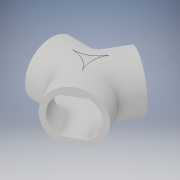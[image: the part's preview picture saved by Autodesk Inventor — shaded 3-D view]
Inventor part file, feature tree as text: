
AUTODESK INVENTOR PART (.ipt)
format: ipt  version: 2017 (Build 210142000, 142)  size: 393,216 bytes
history: native  units: in
note: dims shown in document units (in); Inventor stores cm internally (conversion verified against a paired STEP export)
features: sketch x5, extrude x4, other x2, pattern_circular x2, sweep x2
ambient origin geometry x8: Origin, YZ Plane, XZ Plane, XY Plane, X Axis, Y Axis, Z Axis, Center Point
bodies: Solid1 (feature_tree), Solid2 (feature_tree), Solid3 (feature_tree)
feature tree (15):
  sketch  "Sketch1"  dims[d10=6.6667in d11=4.0in d12=4.0in d13=0.0in d14=9.7746in]
  extrude  "corridor"  Depth=9.7746in
  extrude  "light"  Depth=1.1811in TaperAngle=360.0deg
  other  "found rotaion axis"
  other  "rotaion axis"
  pattern_circular  "other corridors"  Count=3 Angle=360.0deg
  sketch  "Sketch5"  dims[d24=0.0in d25=0.0in d26=1.1811in d27=360.0deg]
  sketch  "Sketch4"  dims[d15=2.8217in d16=1.1811in d17=360.0deg]
  sweep  "curve edjes"
  sweep  "light curve"
  pattern_circular  "repeat curve edjes"  [2 undecoded]
  extrude  "top hole fill in"  Depth=1.429in TaperAngle=0.0deg
  extrude  "bottom hole fill up"  TaperAngle=0.0deg  [1 undecoded]
  sketch  "Sketch7"  dims[d37=1.554in d38=0.0in d46=1.0in]
  sketch  "Sketch9"  dims[d51=0.5833in d52=0.0625in d53=0.0625in d54=0.125in d55=0.0625in d61=0.25in d64=0.0892in d65=0.0884in d67=1.0in d68=0.0in d69=0.0in d70=0.0in d71=1.429in d72=0.0in d74=3.3333in]
note: 3 required parameter values undecoded (feature->parameter linkage not recoverable at this tier; creation-order binding heuristic only, values carry confidence <= 0.55)
